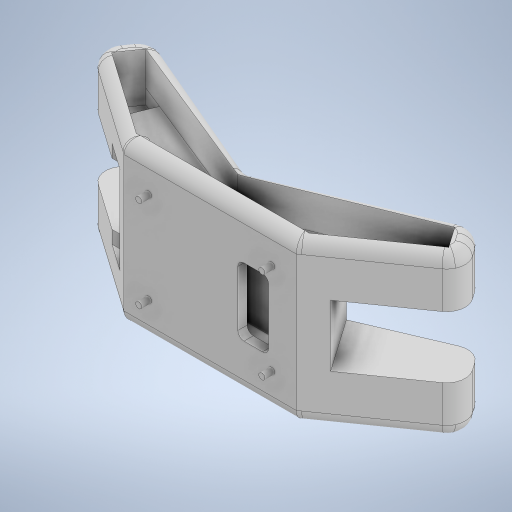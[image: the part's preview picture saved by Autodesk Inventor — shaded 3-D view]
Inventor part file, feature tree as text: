
AUTODESK INVENTOR PART (.ipt)
format: ipt  version: 2024 (Build 280153000, 153)  size: 568,320 bytes
history: native  units: mm
features: extrude x15, sketch x15, fillet x4, other x2
ambient origin geometry x8: Origin, YZ Plane, XZ Plane, XY Plane, X Axis, Y Axis, Z Axis, Center Point
bodies: Body1 (feature_tree)
feature tree (36):
  other  "Těleso1"
  extrude  "Vysunutí1"  Depth=140.0mm
  extrude  "Vysunutí2"  Depth=90.0mm
  extrude  "Vysunutí3"  Depth=30.0mm TaperAngle=0.0deg
  extrude  "Vysunutí7"  Depth=15.0mm
  extrude  "Vysunutí8"  Depth=71.0mm
  extrude  "Vysunutí9"  Depth=132.0mm TaperAngle=0.0deg
  other  "Pracovní rovina1"
  extrude  "Vysunutí10"  Depth=100.0mm
  extrude  "Vysunutí11"  Depth=74.0mm
  extrude  "Vysunutí12"  Depth=5.0mm
  extrude  "Vysunutí13"  Depth=20.0mm
  fillet  "Zaoblení1"  Radius=8.0mm
  fillet  "Zaoblení2"  Radius=100.0mm
  extrude  "Vysunutí14"  Depth=6.108652mm
  extrude  "Vysunutí16"  Depth=35.0mm
  fillet  "Zaoblení3"  Radius=100.0mm
  fillet  "Zaoblení4"  Radius=25.307274mm
  extrude  "Vysunutí17"  Depth=35.0mm
  extrude  "Vysunutí18"  Depth=20.0mm TaperAngle=0.0deg
  extrude  "Vysunutí19"  Depth=160.0mm
  sketch  "Náčrt1"
  sketch  "Náčrt2"
  sketch  "Náčrt3"
  sketch  "Náčrt7"
  sketch  "Náčrt8"
  sketch  "Náčrt9"
  sketch  "Náčrt11"
  sketch  "Náčrt12"
  sketch  "Náčrt13"
  sketch  "Náčrt14"
  sketch  "Náčrt17"
  sketch  "Náčrt19"
  sketch  "Náčrt20"
  sketch  "Náčrt21"
  sketch  "Náčrt23"
